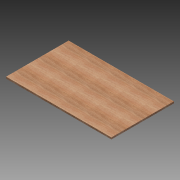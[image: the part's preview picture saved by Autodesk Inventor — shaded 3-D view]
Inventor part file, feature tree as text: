
AUTODESK INVENTOR PART (.ipt)
format: ipt  version: 2013 (Build 170138000, 138)  size: 83,968 bytes
history: native  units: in
note: dims shown in document units (in); Inventor stores cm internally (conversion verified against a paired STEP export)
features: extrude x1, sketch x1
ambient origin geometry x8: Origin, YZ Plane, XZ Plane, XY Plane, X Axis, Y Axis, Z Axis, Center Point
bodies: Solid1 (feature_tree)
feature tree (2):
  extrude  "Extrusion1"  Depth=27.0in
  sketch  "Sketch1"  dims[d18=0.75in d19=0.0in d20=27.0in d21=45.5in]
